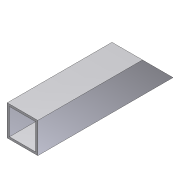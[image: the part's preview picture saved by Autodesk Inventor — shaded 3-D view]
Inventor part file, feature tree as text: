
AUTODESK INVENTOR PART (.ipt)
format: ipt  version: 2012 (Build 160160000, 160)  size: 79,872 bytes
history: native  units: in
note: dims shown in document units (in); Inventor stores cm internally (conversion verified against a paired STEP export)
features: extrude x2, sketch x2, shell x1
ambient origin geometry x8: Origin, YZ Plane, XZ Plane, XY Plane, X Axis, Y Axis, Z Axis, Center Point
bodies: Solid1 (feature_tree)
feature tree (5):
  extrude  "Extrusion1"  Depth=1.75in
  shell  "Shell1"  Thickness=7.75in
  extrude  "Extrusion2"  TaperAngle=45.0deg  [1 undecoded]
  sketch  "Sketch1"  dims[d0=1.75in d1=1.75in d2=7.75in d3=0.0in]
  sketch  "Sketch2"  dims[d4=0.125in d5=45.0deg d6=7.75in d7=0.0in]
note: 1 required parameter value undecoded (feature->parameter linkage not recoverable at this tier; creation-order binding heuristic only, values carry confidence <= 0.55)
